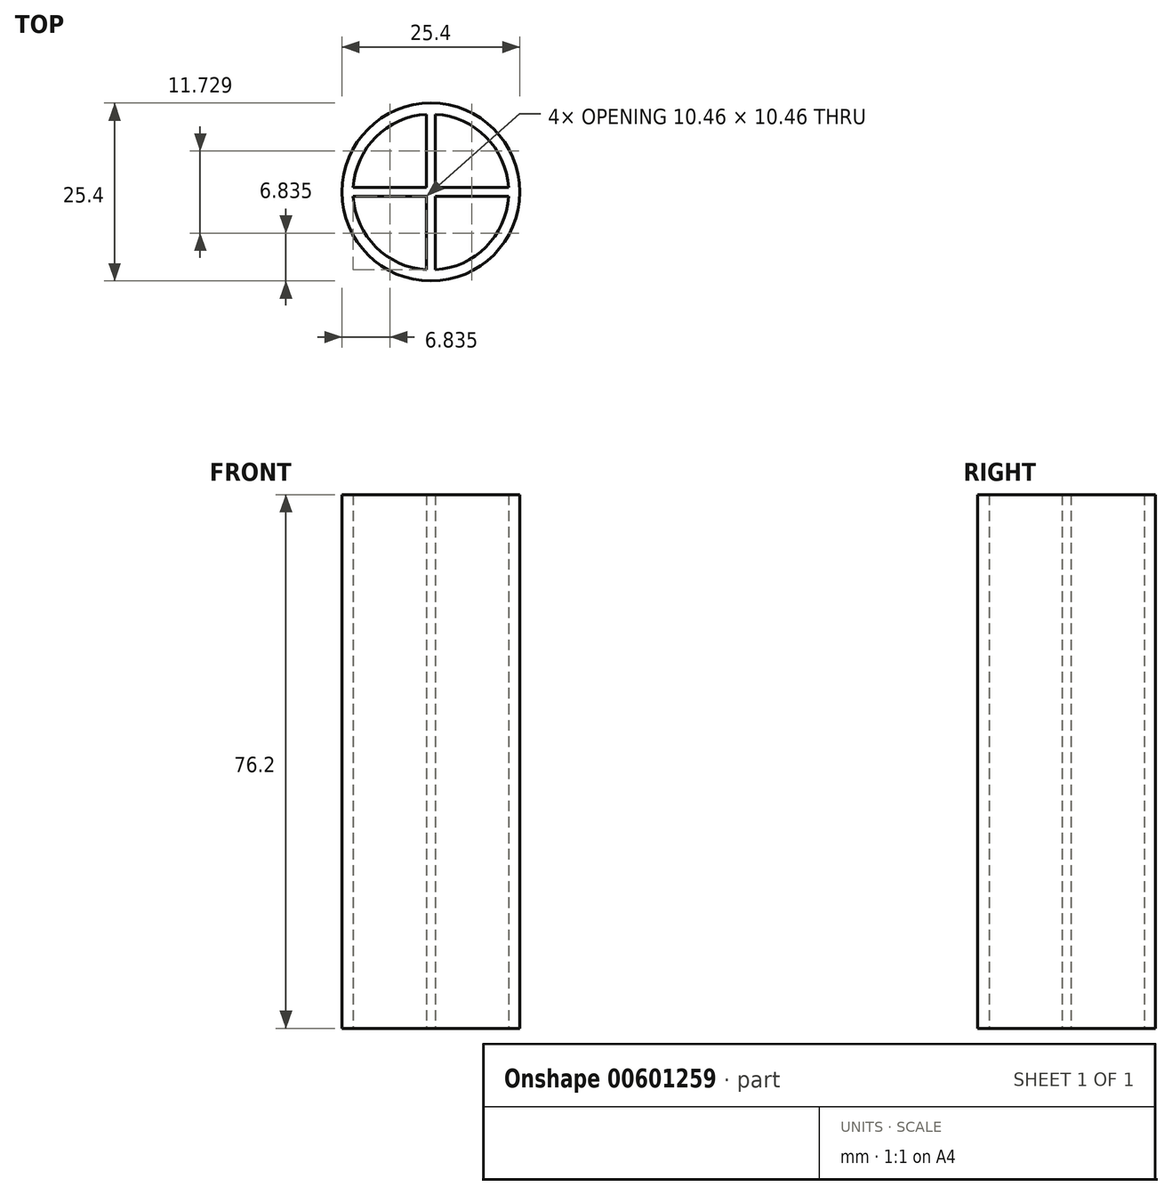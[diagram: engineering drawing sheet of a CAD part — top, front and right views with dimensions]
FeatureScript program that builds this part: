
annotation { "Feature Type Name" : "Feature", "Feature Type Description" : "" }
export const myFeature = defineFeature(function(context is Context, id is Id, definition is map)
    precondition{}
    {
        {
            var Q0;
            Q0=qCreatedBy(makeId("Top.planeOp"),FACE);
            var sketch = newSketch(context, id + "F0", { "sketchPlane" : qUnion([Q0])});
            skCircle(sketch, "E0", {"center": v(0, 0) * mm, "radius": 12.7 * mm});
            skCircle(sketch, "E1", {"center": v(0, 0) * mm, "radius": 11.11 * mm});
            skLineSegment(sketch, "E2.bottom", {"start": v(0.63, 11.11) * mm, "end": v(-0.64, 11.11) * mm});
            skLineSegment(sketch, "E2.top", {"start": v(0.64, -11.11) * mm, "end": v(-0.63, -11.11) * mm});
            skLineSegment(sketch, "E2.left", {"start": v(0.63, 11.11) * mm, "end": v(0.64, -11.11) * mm});
            skLineSegment(sketch, "E2.right", {"start": v(-0.64, 11.11) * mm, "end": v(-0.63, -11.11) * mm});
            skLineSegment(sketch, "E3.bottom", {"start": v(11.11, -0.64) * mm, "end": v(-11.11, -0.64) * mm});
            skLineSegment(sketch, "E3.top", {"start": v(11.11, 0.64) * mm, "end": v(-11.11, 0.63) * mm});
            skLineSegment(sketch, "E3.left", {"start": v(11.11, -0.64) * mm, "end": v(11.11, 0.64) * mm});
            skLineSegment(sketch, "E3.right", {"start": v(-11.11, -0.64) * mm, "end": v(-11.11, 0.64) * mm});
            skSolve(sketch);
        }
        {
            var Q0;
            Q0=makeQuery(id+"F0.imprint","IMPRINT",FACE,{"disambiguationData":[TD([[makeQuery(id+"F0.imprint","IMPRINT",EDGE,{"derivedFrom":sQuery(id+"F0.wireOp",EDGE,"E0")}),1.0]])]});
            var Q1;
            {var subQ1=sQuery(id+"F0.wireOp",EDGE,"E1");var subQ5=sQuery(id+"F0.wireOp",EDGE,"E3.top");var subQ7=makeQuery(id+"F0.imprint","INTERSECT",VERTEX,{"disambiguationData":[OD(1.0)],"derivedFrom":[subQ1,subQ5]});Q1=makeQuery(id+"F0.imprint","IMPRINT",FACE,{"disambiguationData":[TD([[makeQuery(id+"F0.imprint","IMPRINT",EDGE,{"disambiguationData":[TD([[subQ7,-1.0]])],"derivedFrom":subQ1}),1.0]])]});}
            var Q2;
            {var subQ0=sQuery(id+"F0.wireOp",EDGE,"E1");var subQ6=sQuery(id+"F0.wireOp",EDGE,"E2.left");var subQ8=makeQuery(id+"F0.imprint","INTERSECT",VERTEX,{"disambiguationData":[OD(0.0)],"derivedFrom":[subQ0,subQ6]});Q2=makeQuery(id+"F0.imprint","IMPRINT",FACE,{"disambiguationData":[TD([[makeQuery(id+"F0.imprint","IMPRINT",EDGE,{"disambiguationData":[TD([[subQ8,-1.0]])],"derivedFrom":subQ0}),1.0]])]});}
            var Q3;
            {var subQ0=sQuery(id+"F0.wireOp",EDGE,"E2.right");var subQ1=sQuery(id+"F0.wireOp",EDGE,"E1");var subQ2=makeQuery(id+"F0.imprint","INTERSECT",VERTEX,{"disambiguationData":[OD(1.0)],"derivedFrom":[subQ1,subQ0]});Q3=makeQuery(id+"F0.imprint","IMPRINT",FACE,{"disambiguationData":[TD([[makeQuery(id+"F0.imprint","IMPRINT",EDGE,{"disambiguationData":[TD([[subQ2,-1.0]])],"derivedFrom":subQ1}),1.0]])]});}
            var Q4;
            {var subQ1=sQuery(id+"F0.wireOp",EDGE,"E1");var subQ5=sQuery(id+"F0.wireOp",EDGE,"E3.top");var subQ8=makeQuery(id+"F0.imprint","INTERSECT",VERTEX,{"disambiguationData":[OD(0.0)],"derivedFrom":[subQ1,subQ5]});Q4=makeQuery(id+"F0.imprint","IMPRINT",FACE,{"disambiguationData":[TD([[makeQuery(id+"F0.imprint","IMPRINT",EDGE,{"disambiguationData":[TD([[subQ8,1.0]])],"derivedFrom":subQ1}),1.0]])]});}
            var Q5;
            {var subQ0=sQuery(id+"F0.wireOp",EDGE,"E3.top");var subQ1=sQuery(id+"F0.wireOp",EDGE,"E2.left");var subQ2=makeQuery(id+"F0.imprint","INTERSECT",VERTEX,{"derivedFrom":[subQ1,subQ0]});Q5=makeQuery(id+"F0.imprint","IMPRINT",FACE,{"disambiguationData":[TD([[makeQuery(id+"F0.imprint","IMPRINT",EDGE,{"disambiguationData":[TD([[subQ2,-1.0]])],"derivedFrom":subQ1}),-1.0]])]});}
            var Q6;
            {var subQ0=sQuery(id+"F0.wireOp",EDGE,"E2.bottom");var subQ1=sQuery(id+"F0.wireOp",EDGE,"E1");var subQ2=makeQuery(id+"F0.imprint","INTERSECT",VERTEX,{"derivedFrom":[subQ1,subQ0]});Q6=makeQuery(id+"F0.imprint","IMPRINT",FACE,{"disambiguationData":[TD([[makeQuery(id+"F0.imprint","IMPRINT",EDGE,{"disambiguationData":[TD([[subQ2,-1.0]])],"derivedFrom":subQ1}),-1.0]])]});}
            var Q7;
            {var subQ0=sQuery(id+"F0.wireOp",EDGE,"E2.left");var subQ1=sQuery(id+"F0.wireOp",EDGE,"E1");var subQ2=makeQuery(id+"F0.imprint","INTERSECT",VERTEX,{"disambiguationData":[OD(0.0)],"derivedFrom":[subQ1,subQ0]});Q7=makeQuery(id+"F0.imprint","IMPRINT",FACE,{"disambiguationData":[TD([[makeQuery(id+"F0.imprint","IMPRINT",EDGE,{"disambiguationData":[TD([[subQ2,-1.0]])],"derivedFrom":subQ1}),-1.0]])]});}
            var Q8;
            {var subQ0=sQuery(id+"F0.wireOp",EDGE,"E3.top");var subQ1=sQuery(id+"F0.wireOp",EDGE,"E1");var subQ2=makeQuery(id+"F0.imprint","INTERSECT",VERTEX,{"disambiguationData":[OD(1.0)],"derivedFrom":[subQ1,subQ0]});Q8=makeQuery(id+"F0.imprint","IMPRINT",FACE,{"disambiguationData":[TD([[makeQuery(id+"F0.imprint","IMPRINT",EDGE,{"disambiguationData":[TD([[subQ2,-1.0]])],"derivedFrom":subQ1}),-1.0]])]});}
            var Q9;
            {var subQ0=sQuery(id+"F0.wireOp",EDGE,"E3.right");var subQ1=sQuery(id+"F0.wireOp",EDGE,"E1");var subQ2=makeQuery(id+"F0.imprint","INTERSECT",VERTEX,{"derivedFrom":[subQ1,subQ0]});Q9=makeQuery(id+"F0.imprint","IMPRINT",FACE,{"disambiguationData":[TD([[makeQuery(id+"F0.imprint","IMPRINT",EDGE,{"disambiguationData":[TD([[subQ2,-1.0]])],"derivedFrom":subQ1}),-1.0]])]});}
            var Q10;
            {var subQ0=sQuery(id+"F0.wireOp",EDGE,"E3.left");var subQ1=sQuery(id+"F0.wireOp",EDGE,"E1");var subQ2=makeQuery(id+"F0.imprint","INTERSECT",VERTEX,{"derivedFrom":[subQ1,subQ0]});Q10=makeQuery(id+"F0.imprint","IMPRINT",FACE,{"disambiguationData":[TD([[makeQuery(id+"F0.imprint","IMPRINT",EDGE,{"disambiguationData":[TD([[subQ2,1.0]])],"derivedFrom":subQ1}),-1.0]])]});}
            var Q11;
            {var subQ0=sQuery(id+"F0.wireOp",EDGE,"E3.top");var subQ1=sQuery(id+"F0.wireOp",EDGE,"E1");var subQ2=makeQuery(id+"F0.imprint","INTERSECT",VERTEX,{"disambiguationData":[OD(0.0)],"derivedFrom":[subQ1,subQ0]});Q11=makeQuery(id+"F0.imprint","IMPRINT",FACE,{"disambiguationData":[TD([[makeQuery(id+"F0.imprint","IMPRINT",EDGE,{"disambiguationData":[TD([[subQ2,1.0]])],"derivedFrom":subQ1}),-1.0]])]});}
            var Q12;
            {var subQ0=sQuery(id+"F0.wireOp",EDGE,"E2.top");var subQ1=sQuery(id+"F0.wireOp",EDGE,"E1");var subQ2=makeQuery(id+"F0.imprint","INTERSECT",VERTEX,{"derivedFrom":[subQ1,subQ0]});Q12=makeQuery(id+"F0.imprint","IMPRINT",FACE,{"disambiguationData":[TD([[makeQuery(id+"F0.imprint","IMPRINT",EDGE,{"disambiguationData":[TD([[subQ2,-1.0]])],"derivedFrom":subQ1}),-1.0]])]});}
            var Q13;
            {var subQ0=sQuery(id+"F0.wireOp",EDGE,"E2.right");var subQ1=sQuery(id+"F0.wireOp",EDGE,"E1");var subQ2=makeQuery(id+"F0.imprint","INTERSECT",VERTEX,{"disambiguationData":[OD(1.0)],"derivedFrom":[subQ1,subQ0]});Q13=makeQuery(id+"F0.imprint","IMPRINT",FACE,{"disambiguationData":[TD([[makeQuery(id+"F0.imprint","IMPRINT",EDGE,{"disambiguationData":[TD([[subQ2,-1.0]])],"derivedFrom":subQ1}),-1.0]])]});}
            extrude(context, id + "F1", {"entities" : qUnion([Q0, Q1, Q2, Q3, Q4, Q5, Q6, Q7, Q8, Q9, Q10, Q11, Q12, Q13]), "endBound" : BoundingType.SYMMETRIC, "depth" : 76.2 * mm, "offsetDistance" : 25.4 * mm});
        }
    });
